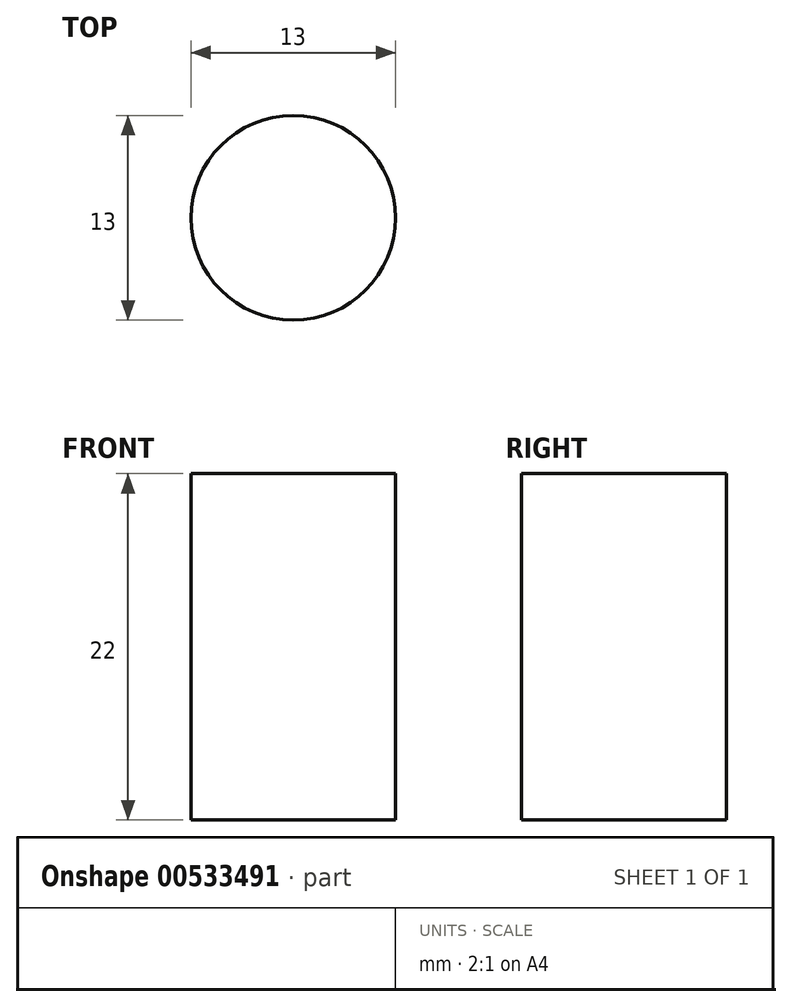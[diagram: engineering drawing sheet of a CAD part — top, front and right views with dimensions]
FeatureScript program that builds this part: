
annotation { "Feature Type Name" : "Feature", "Feature Type Description" : "" }
export const myFeature = defineFeature(function(context is Context, id is Id, definition is map)
    precondition{}
    {
        {
            var Q0;
            Q0=qCreatedBy(makeId("Top.planeOp"),FACE);
            var sketch = newSketch(context, id + "F0", { "sketchPlane" : qUnion([Q0])});
            skCircle(sketch, "E0", {"center": v(0, 0) * mm, "radius": 6.5 * mm});
            skSolve(sketch);
        }
        {
            var Q0;
            Q0=qSketchRegion(id+"F0",true);
            extrude(context, id + "F1", {"entities" : qUnion([Q0]), "depth" : 22 * mm, "offsetDistance" : 25 * mm});
        }
    });
